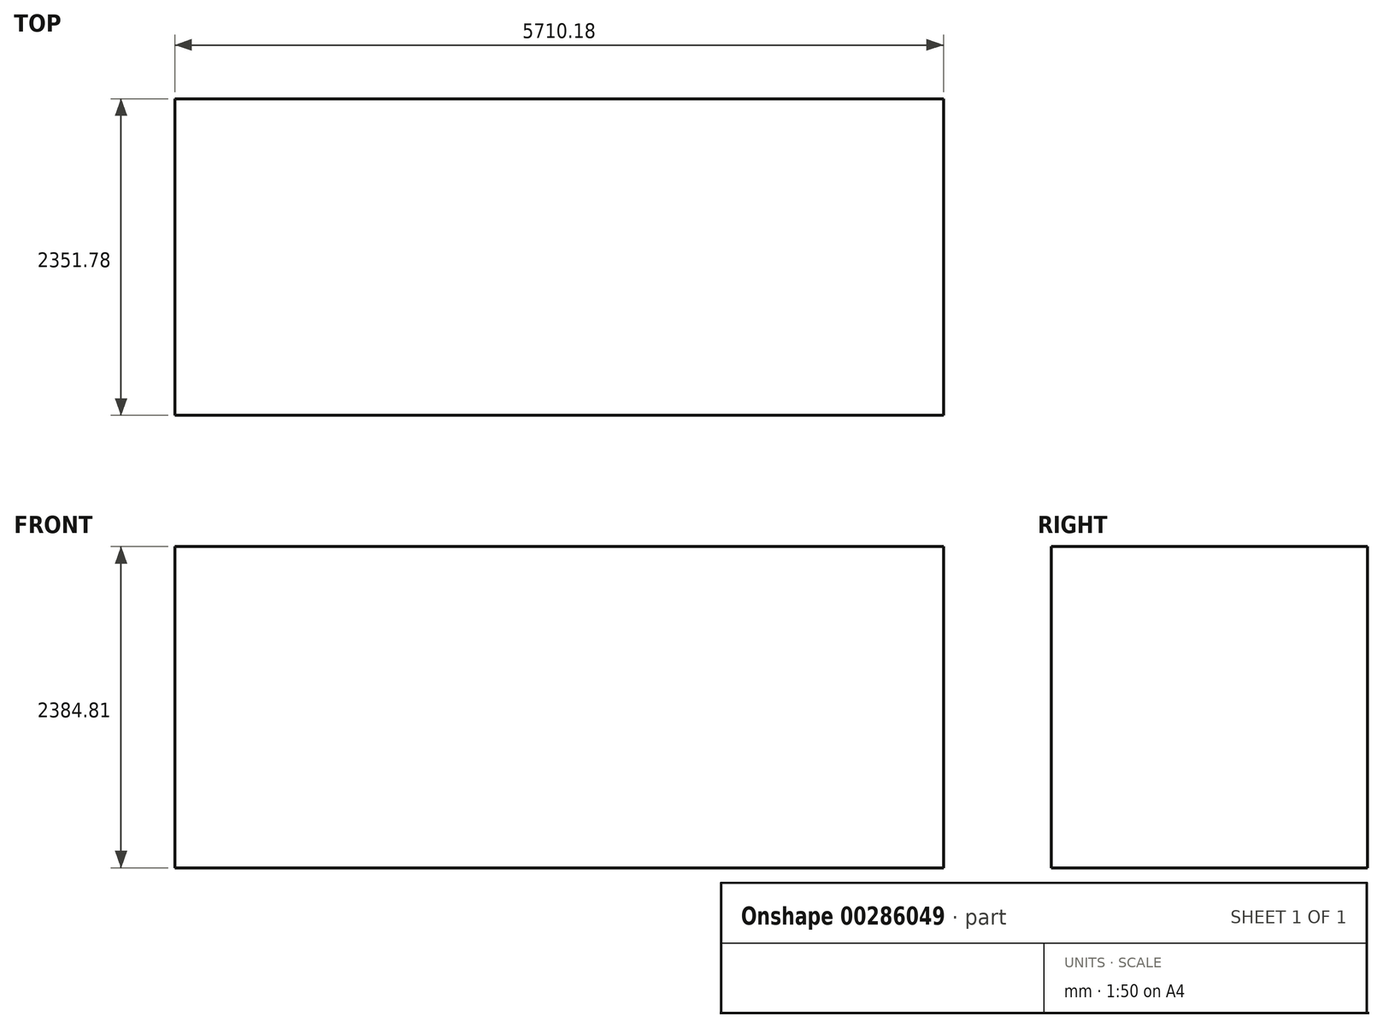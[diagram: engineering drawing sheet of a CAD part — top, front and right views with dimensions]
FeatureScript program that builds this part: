
annotation { "Feature Type Name" : "Feature", "Feature Type Description" : "" }
export const myFeature = defineFeature(function(context is Context, id is Id, definition is map)
    precondition{}
    {
        {
            var Q0;
            Q0=qCreatedBy(makeId("Top.planeOp"),FACE);
            var sketch = newSketch(context, id + "F0", { "sketchPlane" : qUnion([Q0])});
            skLineSegment(sketch, "E0.bottom", {"start": v(2855.09, -1175.9) * mm, "end": v(-2855.09, -1175.9) * mm});
            skLineSegment(sketch, "E0.top", {"start": v(2855.09, 1175.9) * mm, "end": v(-2855.09, 1175.9) * mm});
            skLineSegment(sketch, "E0.left", {"start": v(2855.09, -1175.9) * mm, "end": v(2855.09, 1175.9) * mm});
            skLineSegment(sketch, "E0.right", {"start": v(-2855.09, -1175.9) * mm, "end": v(-2855.09, 1175.9) * mm});
            skPoint(sketch, "E0.middle", {"position": v(0, 0) * mm});
            skSolve(sketch);
        }
        {
            var Q0;
            Q0 = qSketchRegion(id + "F0", true);
            extrude(context, id + "F1", {"entities" : qUnion([Q0]), "depth" : 2384.8 * mm});
        }
    });
